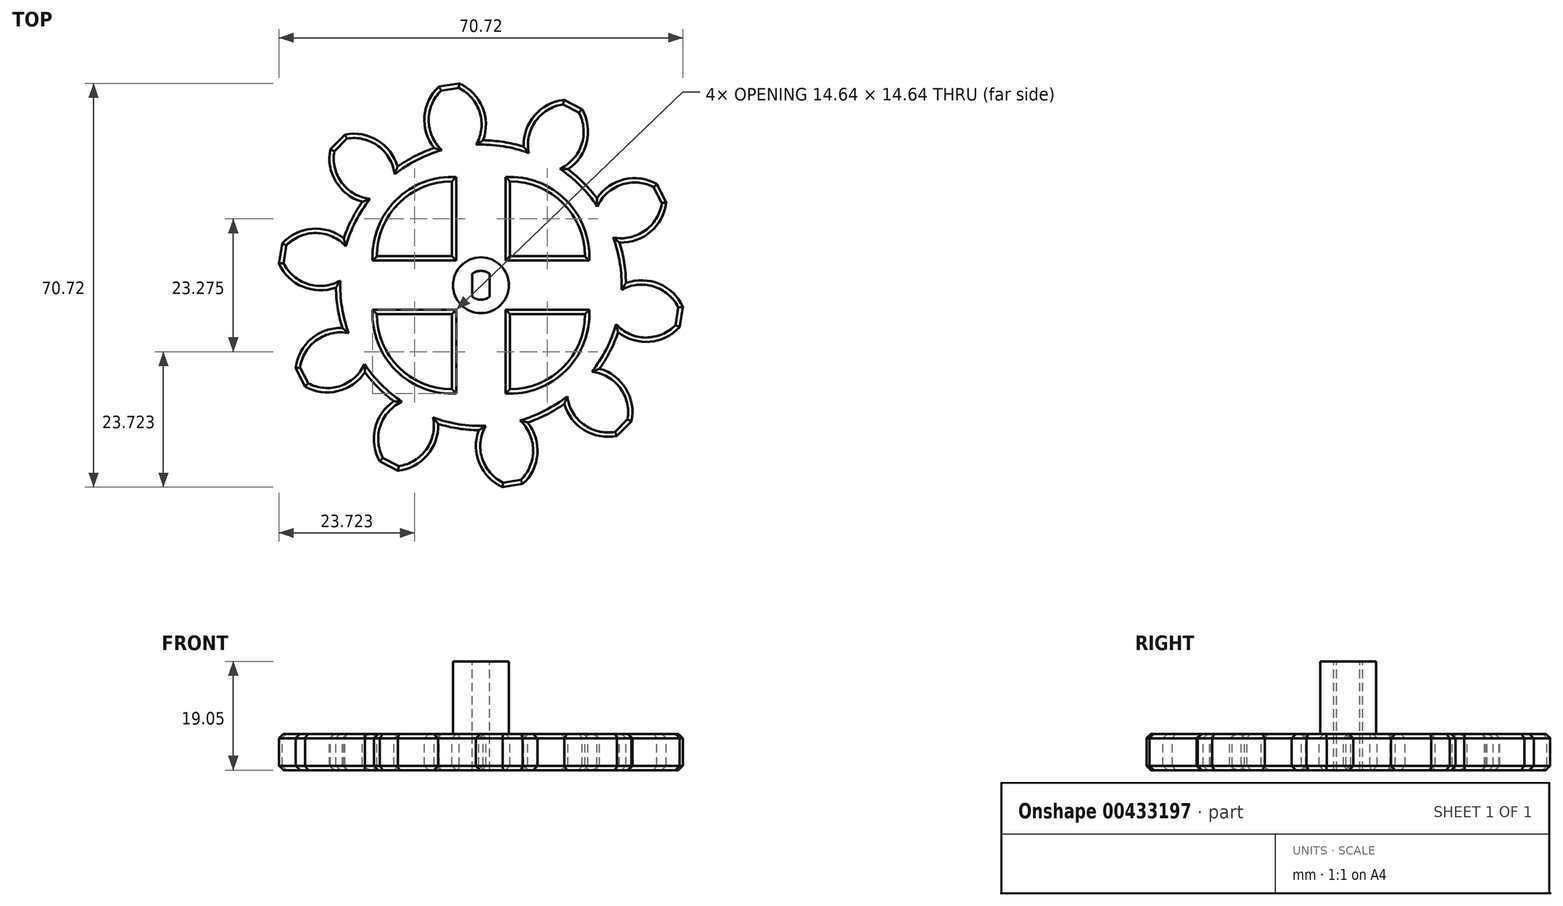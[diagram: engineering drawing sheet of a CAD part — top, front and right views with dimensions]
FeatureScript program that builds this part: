
annotation { "Feature Type Name" : "Feature", "Feature Type Description" : "" }
export const myFeature = defineFeature(function(context is Context, id is Id, definition is map)
    precondition{}
    {
        {
            var Q0;
            Q0=qCreatedBy(makeId("Top.planeOp"),FACE);
            var sketch = newSketch(context, id + "F0", { "sketchPlane" : qUnion([Q0])});
            skCircle(sketch, "E0", {"center": v(0, 0) * mm, "radius": 30.48 * mm, "construction": true});
            skSolve(sketch);
        }
        {
            var Q0;
            Q0=qCreatedBy(makeId("Top.planeOp"),FACE);
            var sketch = newSketch(context, id + "F1", { "sketchPlane" : qUnion([Q0])});
            skCircle(sketch, "E1", {"center": v(0, 0) * mm, "radius": 35.56 * mm, "construction": true});
            skCircle(sketch, "E2", {"center": v(0, 0) * mm, "radius": 31.75 * mm, "construction": true});
            skCircle(sketch, "E3", {"center": v(0, 0) * mm, "radius": 25.4 * mm, "construction": true});
            skLineSegment(sketch, "E4", {"start": v(0, 0) * mm, "end": v(0, 82.3) * mm, "construction": true});
            skLineSegment(sketch, "E5", {"start": v(0, 0) * mm, "end": v(-12.5, 78.88) * mm, "construction": true});
            skLineSegment(sketch, "E6", {"start": v(0, 31.75) * mm, "end": v(-65.71, 31.75) * mm, "construction": true});
            skLineSegment(sketch, "E7", {"start": v(0, 31.75) * mm, "end": v(-58.85, 5.55) * mm, "construction": true});
            skCircle(sketch, "E8", {"center": v(0, 31.75) * mm, "radius": 7.94 * mm, "construction": true});
            skCircle(sketch, "E9", {"center": v(0, 0) * mm, "radius": 29 * mm, "construction": true});
            skCircle(sketch, "E10", {"center": v(-7.06, 28.13) * mm, "radius": 7.94 * mm, "construction": true});
            skArc(sketch, "E11", {"start": v(0.39, 25.4) * mm, "mid": v(0.26, 31.2) * mm, "end": v(-3.78, 35.36) * mm});
            skArc(sketch, "E12.MirrorCS", {"start": v(-8.22, 24.03) * mm, "mid": v(-9.88, 29.59) * mm, "end": v(-7.33, 34.8) * mm});
            skLineSegment(sketch, "E13", {"start": v(-7.33, 34.8) * mm, "end": v(-3.78, 35.36) * mm});
            skArc(sketch, "E14", {"start": v(-8.22, 24.03) * mm, "mid": v(3.97, -25.09) * mm, "end": v(0.39, 25.4) * mm});
            skSolve(sketch);
        }
        {
            var Q0;
            Q0=qSketchRegion(id+"F1",true);
            var Q1;
            Q1=makeQuery(id+"Ffi0VH93psu6soF_0.opExtrude","CAP_FACE",FACE,{"disambiguationData":[OSD([sQuery(id+"F0.wireOp",EDGE,"E0")])],"isStart":true});
            extrude(context, id + "F2", {"entities" : qUnion([Q0]), "oppositeDirection" : true, "endBoundEntityFace" : qUnion([Q1]), "depth" : 6.35 * mm});
        }
        {
            var Q0;
            Q0=makeQuery(id+"F2.opExtrude","SWEPT_BODY",BODY,{"disambiguationData":[OSD([sQuery(id+"F1.wireOp",EDGE,"E11"),sQuery(id+"F1.wireOp",EDGE,"E12.MirrorCS"),sQuery(id+"F1.wireOp",EDGE,"E13"),sQuery(id+"F1.wireOp",EDGE,"ZPE7Z8ba-rLlS-d3gG-Tl0h-fifcE816pJjn")])]});
            var Q1;
            Q1=sQuery(id+"F0.wireOp",EDGE,"E0");
            circularPattern(context, id + "F3", {"operationType" : NewBodyOperationType.ADD, "entities" : qUnion([Q0]), "axis" : qUnion([Q1]), "angle" : 360 * degree, "instanceCount" : 10, "equalSpace" : true});
        }
        {
            var Q0;
            {var subQ0=makeQuery(id+"F2.opExtrude","CAP_FACE",FACE,{"disambiguationData":[OSD([sQuery(id+"F1.wireOp",EDGE,"E11"),sQuery(id+"F1.wireOp",EDGE,"E12.MirrorCS"),sQuery(id+"F1.wireOp",EDGE,"E13"),sQuery(id+"F1.wireOp",EDGE,"ZPE7Z8ba-rLlS-d3gG-Tl0h-fifcE816pJjn")])],"isStart":true});Q0=makeQuery(id+"F3.boolean.opBoolean","MERGE",FACE,{"derivedFrom":[makeQuery(id+"Ffi0VH93psu6soF_0.opExtrude","CAP_FACE",FACE,{"disambiguationData":[OSD([sQuery(id+"F0.wireOp",EDGE,"E0")])],"isStart":false}),subQ0,makeQuery(id+"F3.opPattern","COPY",FACE,{"derivedFrom":subQ0,"instanceName":"1"}),makeQuery(id+"F3.opPattern","COPY",FACE,{"derivedFrom":subQ0,"instanceName":"2"}),makeQuery(id+"F3.opPattern","COPY",FACE,{"derivedFrom":subQ0,"instanceName":"3"}),makeQuery(id+"F3.opPattern","COPY",FACE,{"derivedFrom":subQ0,"instanceName":"4"}),makeQuery(id+"F3.opPattern","COPY",FACE,{"derivedFrom":subQ0,"instanceName":"5"}),makeQuery(id+"F3.opPattern","COPY",FACE,{"derivedFrom":subQ0,"instanceName":"6"}),makeQuery(id+"F3.opPattern","COPY",FACE,{"derivedFrom":subQ0,"instanceName":"7"}),makeQuery(id+"F3.opPattern","COPY",FACE,{"derivedFrom":subQ0,"instanceName":"8"}),makeQuery(id+"F3.opPattern","COPY",FACE,{"derivedFrom":subQ0,"instanceName":"9"}),makeQuery(id+"F3.opPattern","COPY",FACE,{"derivedFrom":subQ0,"instanceName":"10"}),makeQuery(id+"F3.opPattern","COPY",FACE,{"derivedFrom":subQ0,"instanceName":"11"}),makeQuery(id+"F3.opPattern","COPY",FACE,{"derivedFrom":subQ0,"instanceName":"12"}),makeQuery(id+"F3.opPattern","COPY",FACE,{"derivedFrom":subQ0,"instanceName":"13"}),makeQuery(id+"F3.opPattern","COPY",FACE,{"derivedFrom":subQ0,"instanceName":"14"})]});}
            var sketch = newSketch(context, id + "F4", { "sketchPlane" : qUnion([Q0])});
            skLineSegment(sketch, "E15", {"start": v(-5.08, 5.08) * mm, "end": v(-18.22, 5.08) * mm});
            skLineSegment(sketch, "E16", {"start": v(-5.08, 5.08) * mm, "end": v(-5.08, 18.22) * mm});
            skArc(sketch, "E17", {"start": v(-5.08, 18.22) * mm, "mid": v(-14.37, 14.37) * mm, "end": v(-18.22, 5.08) * mm});
            skArc(sketch, "E18.1.0", {"start": v(-18.22, -5.08) * mm, "mid": v(-14.37, -14.37) * mm, "end": v(-5.08, -18.22) * mm});
            skLineSegment(sketch, "E18.1.1", {"start": v(-5.08, -5.08) * mm, "end": v(-18.22, -5.08) * mm});
            skLineSegment(sketch, "E18.1.2", {"start": v(-5.08, -5.08) * mm, "end": v(-5.08, -18.22) * mm});
            skArc(sketch, "E18.2.0", {"start": v(5.08, -18.22) * mm, "mid": v(14.37, -14.37) * mm, "end": v(18.22, -5.08) * mm});
            skLineSegment(sketch, "E18.2.1", {"start": v(5.08, -5.08) * mm, "end": v(5.08, -18.22) * mm});
            skLineSegment(sketch, "E18.2.2", {"start": v(5.08, -5.08) * mm, "end": v(18.22, -5.08) * mm});
            skArc(sketch, "E18.3.0", {"start": v(18.22, 5.08) * mm, "mid": v(14.37, 14.37) * mm, "end": v(5.08, 18.22) * mm});
            skLineSegment(sketch, "E18.3.1", {"start": v(5.08, 5.08) * mm, "end": v(18.22, 5.08) * mm});
            skLineSegment(sketch, "E18.3.2", {"start": v(5.08, 5.08) * mm, "end": v(5.08, 18.22) * mm});
            skPoint(sketch, "E18.center", {"position": v(0, 0) * mm});
            skSolve(sketch);
        }
        {
            var Q0;
            Q0=qSketchRegion(id+"F4",true);
            extrude(context, id + "F5", {"entities" : qUnion([Q0]), "operationType" : NewBodyOperationType.REMOVE, "endBound" : BoundingType.THROUGH_ALL, "oppositeDirection" : true, "depth" : 25.4 * mm});
        }
        {
            var Q0;
            {var subQ0=makeQuery(id+"F2.opExtrude","CAP_FACE",FACE,{"disambiguationData":[OSD([sQuery(id+"F1.wireOp",EDGE,"E11"),sQuery(id+"F1.wireOp",EDGE,"E12.MirrorCS"),sQuery(id+"F1.wireOp",EDGE,"E13"),sQuery(id+"F1.wireOp",EDGE,"E14")])],"isStart":true});Q0=makeQuery(id+"F3.boolean.opBoolean","MERGE",FACE,{"derivedFrom":[subQ0,makeQuery(id+"F3.opPattern","COPY",FACE,{"derivedFrom":subQ0,"instanceName":"1"}),makeQuery(id+"F3.opPattern","COPY",FACE,{"derivedFrom":subQ0,"instanceName":"2"}),makeQuery(id+"F3.opPattern","COPY",FACE,{"derivedFrom":subQ0,"instanceName":"3"}),makeQuery(id+"F3.opPattern","COPY",FACE,{"derivedFrom":subQ0,"instanceName":"4"}),makeQuery(id+"F3.opPattern","COPY",FACE,{"derivedFrom":subQ0,"instanceName":"5"}),makeQuery(id+"F3.opPattern","COPY",FACE,{"derivedFrom":subQ0,"instanceName":"6"}),makeQuery(id+"F3.opPattern","COPY",FACE,{"derivedFrom":subQ0,"instanceName":"7"}),makeQuery(id+"F3.opPattern","COPY",FACE,{"derivedFrom":subQ0,"instanceName":"8"}),makeQuery(id+"F3.opPattern","COPY",FACE,{"derivedFrom":subQ0,"instanceName":"9"})]});}
            var Q1;
            {var subQ0=makeQuery(id+"F2.opExtrude","CAP_FACE",FACE,{"disambiguationData":[OSD([sQuery(id+"F1.wireOp",EDGE,"E11"),sQuery(id+"F1.wireOp",EDGE,"E12.MirrorCS"),sQuery(id+"F1.wireOp",EDGE,"E13"),sQuery(id+"F1.wireOp",EDGE,"E14")])],"isStart":false});Q1=makeQuery(id+"F3.boolean.opBoolean","MERGE",FACE,{"derivedFrom":[subQ0,makeQuery(id+"F3.opPattern","COPY",FACE,{"derivedFrom":subQ0,"instanceName":"1"}),makeQuery(id+"F3.opPattern","COPY",FACE,{"derivedFrom":subQ0,"instanceName":"2"}),makeQuery(id+"F3.opPattern","COPY",FACE,{"derivedFrom":subQ0,"instanceName":"3"}),makeQuery(id+"F3.opPattern","COPY",FACE,{"derivedFrom":subQ0,"instanceName":"4"}),makeQuery(id+"F3.opPattern","COPY",FACE,{"derivedFrom":subQ0,"instanceName":"5"}),makeQuery(id+"F3.opPattern","COPY",FACE,{"derivedFrom":subQ0,"instanceName":"6"}),makeQuery(id+"F3.opPattern","COPY",FACE,{"derivedFrom":subQ0,"instanceName":"7"}),makeQuery(id+"F3.opPattern","COPY",FACE,{"derivedFrom":subQ0,"instanceName":"8"}),makeQuery(id+"F3.opPattern","COPY",FACE,{"derivedFrom":subQ0,"instanceName":"9"})]});}
            chamfer(context, id + "F6", {"entities" : qUnion([Q0, Q1]), "width" : 0.76 * mm, "tangentPropagation" : true});
        }
        {
            var Q0;
            {var subQ0=makeQuery(id+"F2.opExtrude","CAP_FACE",FACE,{"disambiguationData":[OSD([sQuery(id+"F1.wireOp",EDGE,"E11"),sQuery(id+"F1.wireOp",EDGE,"E12.MirrorCS"),sQuery(id+"F1.wireOp",EDGE,"E13"),sQuery(id+"F1.wireOp",EDGE,"E14")])],"isStart":true});Q0=makeQuery(id+"F3.boolean.opBoolean","MERGE",FACE,{"derivedFrom":[subQ0,makeQuery(id+"F3.opPattern","COPY",FACE,{"derivedFrom":subQ0,"instanceName":"1"}),makeQuery(id+"F3.opPattern","COPY",FACE,{"derivedFrom":subQ0,"instanceName":"2"}),makeQuery(id+"F3.opPattern","COPY",FACE,{"derivedFrom":subQ0,"instanceName":"3"}),makeQuery(id+"F3.opPattern","COPY",FACE,{"derivedFrom":subQ0,"instanceName":"4"}),makeQuery(id+"F3.opPattern","COPY",FACE,{"derivedFrom":subQ0,"instanceName":"5"}),makeQuery(id+"F3.opPattern","COPY",FACE,{"derivedFrom":subQ0,"instanceName":"6"}),makeQuery(id+"F3.opPattern","COPY",FACE,{"derivedFrom":subQ0,"instanceName":"7"}),makeQuery(id+"F3.opPattern","COPY",FACE,{"derivedFrom":subQ0,"instanceName":"8"}),makeQuery(id+"F3.opPattern","COPY",FACE,{"derivedFrom":subQ0,"instanceName":"9"})]});}
            var sketch = newSketch(context, id + "F7", { "sketchPlane" : qUnion([Q0])});
            skCircle(sketch, "E19", {"center": v(0, 0) * mm, "radius": 4.89 * mm});
            skSolve(sketch);
        }
        {
            var Q0;
            Q0=qSketchRegion(id+"F7",true);
            extrude(context, id + "F8", {"entities" : qUnion([Q0]), "operationType" : NewBodyOperationType.ADD, "depth" : 12.7 * mm, "offsetDistance" : 25.4 * mm});
        }
        {
            var Q0;
            Q0=makeQuery(id+"F8.opExtrude","CAP_FACE",FACE,{"disambiguationData":[OSD([sQuery(id+"F7.wireOp",EDGE,"E19")])],"isStart":false});
            var sketch = newSketch(context, id + "F9", { "sketchPlane" : qUnion([Q0])});
            skArc(sketch, "E20", {"start": v(-1.52, -2.03) * mm, "mid": v(0, -2.54) * mm, "end": v(1.52, -2.03) * mm});
            skLineSegment(sketch, "E21", {"start": v(1.52, 2.03) * mm, "end": v(1.52, -2.03) * mm});
            skLineSegment(sketch, "E22", {"start": v(-1.52, 2.03) * mm, "end": v(-1.52, -2.03) * mm});
            skArc(sketch, "E23.trimOffspring", {"start": v(1.52, 2.03) * mm, "mid": v(0, 2.54) * mm, "end": v(-1.52, 2.03) * mm});
            skSolve(sketch);
        }
        {
            var Q0;
            Q0=qSketchRegion(id+"F9",true);
            extrude(context, id + "F10", {"entities" : qUnion([Q0]), "operationType" : NewBodyOperationType.REMOVE, "oppositeDirection" : true, "depth" : 25.4 * mm});
        }
    });
